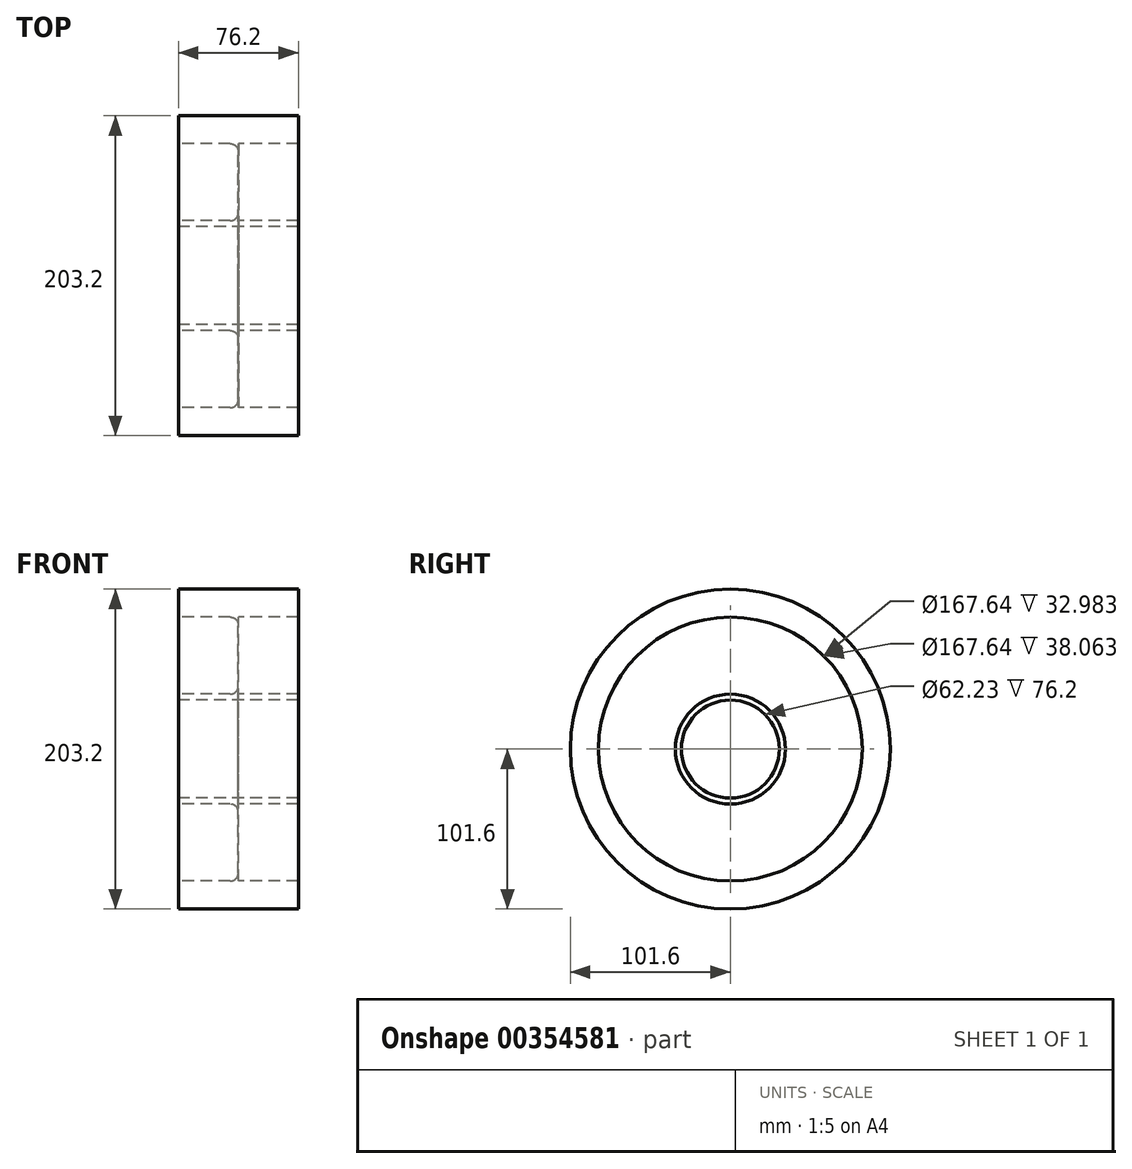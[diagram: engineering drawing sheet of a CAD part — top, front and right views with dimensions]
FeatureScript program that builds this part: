
annotation { "Feature Type Name" : "Feature", "Feature Type Description" : "" }
export const myFeature = defineFeature(function(context is Context, id is Id, definition is map)
    precondition{}
    {
        {
            var Q0;
            Q0=qCreatedBy(makeId("Right.planeOp"),FACE);
            var sketch = newSketch(context, id + "F0", { "sketchPlane" : qUnion([Q0])});
            skCircle(sketch, "E0", {"center": v(0, 0) * mm, "radius": 101.6 * mm});
            skCircle(sketch, "E1", {"center": v(0, 0) * mm, "radius": 31.12 * mm});
            skCircle(sketch, "E2", {"center": v(0, 0) * mm, "radius": 83.82 * mm});
            skCircle(sketch, "E3", {"center": v(0, 0) * mm, "radius": 34.93 * mm});
            skSolve(sketch);
        }
        {
            var Q0;
            Q0=makeQuery(id+"F0.imprint","IMPRINT",FACE,{"disambiguationData":[TD([[makeQuery(id+"F0.imprint","IMPRINT",EDGE,{"derivedFrom":sQuery(id+"F0.wireOp",EDGE,"E0")}),1.0]])]});
            var Q1;
            Q1=makeQuery(id+"F0.imprint","IMPRINT",FACE,{"disambiguationData":[TD([[makeQuery(id+"F0.imprint","IMPRINT",EDGE,{"derivedFrom":sQuery(id+"F0.wireOp",EDGE,"E1")}),-1.0]])]});
            extrude(context, id + "F1", {"entities" : qUnion([Q0, Q1]), "depth" : 38.1 * mm, "hasSecondDirection" : true, "secondDirectionOppositeDirection" : true, "secondDirectionDepth" : 38.1 * mm});
        }
        {
            var Q0;
            Q0=makeQuery(id+"F0.imprint","IMPRINT",FACE,{"disambiguationData":[TD([[makeQuery(id+"F0.imprint","IMPRINT",EDGE,{"derivedFrom":sQuery(id+"F0.wireOp",EDGE,"E2")}),1.0]])]});
            extrude(context, id + "F2", {"entities" : qUnion([Q0]), "operationType" : NewBodyOperationType.ADD, "depth" : (3 - 1.1) / 50.8 * mm, "hasSecondDirection" : true, "secondDirectionOppositeDirection" : true, "secondDirectionDepth" : (3 - 1.1) / 50.8 * mm});
        }
        {
            var Q0;
            Q0=makeQuery(id+"F2.opExtrude","CAP_EDGE",EDGE,{"disambiguationData":[OSD([sQuery(id+"F0.wireOp",EDGE,"E3")])],"isStart":false});
            var Q1;
            Q1=makeQuery(id+"F2.opExtrude","CAP_EDGE",EDGE,{"disambiguationData":[OSD([sQuery(id+"F0.wireOp",EDGE,"E2")])],"isStart":false});
            var Q2;
            Q2=makeQuery(id+"F2.opExtrude","CAP_EDGE",EDGE,{"disambiguationData":[OSD([sQuery(id+"F0.wireOp",EDGE,"E3")])],"isStart":true});
            var Q3;
            Q3=makeQuery(id+"F2.opExtrude","CAP_EDGE",EDGE,{"disambiguationData":[OSD([sQuery(id+"F0.wireOp",EDGE,"E2")])],"isStart":true});
            fillet(context, id + "F3", {"entities" : qUnion([Q0, Q1, Q2, Q3]), "radius" : 5.08 * mm, "tangentPropagation" : true, "allowEdgeOverflow" : false});
        }
    });
